# Revit family: MT-HB_SLIDING DOOR_XX
name_source: partatom
category: Doors
revit_build: Autodesk Revit 2017 (Build: 20160225_1515(x64)
units: mm (PartAtom-declared; Revit-internal decimal feet)

## family parameters
Always vertical = Yes
Cut with Voids When Loaded = No
Host = Wall
OmniClass Number = 23.30.20.00
OmniClass Title = Windows
Room Calculation Point = No
Shared = No

## types (2) — shared parameters
AIR POCKET = 5 mm  [stored 0.0164042 ft]
ANZRC COMPLIANT = YES
Analytic Construction = <None>
DOUBLE GLAZED THICKNESS = 18 mm  [stored 0.0590551 ft]
FRAME MATERIAL = <By Category>
GLAZED MATERIAL = Glass
Height = 2100 mm  [stored 6.88976 ft]
MAX HEIGHT = 3000 mm  [stored 9.84252 ft]
MAX PANEL HEIGHT = 3000 mm  [stored 9.84252 ft]
MAX PANEL WIDTH = 1000 mm  [stored 3.28084 ft]
MAX WIDTH = 2500 mm  [stored 8.2021 ft]
Manufacturer = ALSPEC
Model = HAWKESBURY TOP HUNG COMMERCIAL SLIDING DOOR
OFFSET = 10 mm  [stored 0.0328084 ft]
OVERALL FRAME HEIGHT = 2100 mm  [stored 6.88976 ft]
OVERALL FRAME WIDTH = 2000 mm  [stored 6.56168 ft]
PANEL WIDTH = 962 mm
PANEL WIDTH B = 1046 mm
SINGLE GLAZED THICKNESS = 5 mm  [stored 0.0164042 ft]
URL = WWW.ALSPEC.COM.AU
VERSION = 2.1
WARNING = No
Wall Closure = By host
Width = 2000 mm  [stored 6.56168 ft]
YEAR = 2019
zero-valued in all types: Default Sill Height

## per-type parameters (varying)
| type | 1L1R | 2L/2R | BOT PANEL POSITION | DETAIL_DEPTH SILL | DOUBLE GLAZED | FRAME THICKNESS | PANEL HEIGHT | Rough Height | Rough Width | SILL_TYPE 01 | SILL_TYPE 02 | TOLERANCE | TOP PANEL POSITION |
| 2L/2R | No | Yes | 10 mm  [stored 0.0328084 ft] | 150 mm | No | 76 mm  [stored 0.249344 ft] | 2015 mm | 2200 mm | 2100 mm  [stored 6.88976 ft] | No | Yes | 50 mm  [stored 0.164042 ft] | 1999 mm |
| 1L1R | Yes | No | 35 mm  [stored 0.114829 ft] | 102 mm | Yes | 102 mm | 1990 mm | 2100 mm  [stored 6.88976 ft] | 2000 mm  [stored 6.56168 ft] | Yes | No | 0 mm  [stored 0 ft] | 1974 mm |

note: [stored X ft] marks values corroborated as IEEE doubles in the binary element streams (Revit-internal decimal feet)

## geometry (parser evidence)
native form markers: Sweep x36
no freeform markers — native parametric forms only
